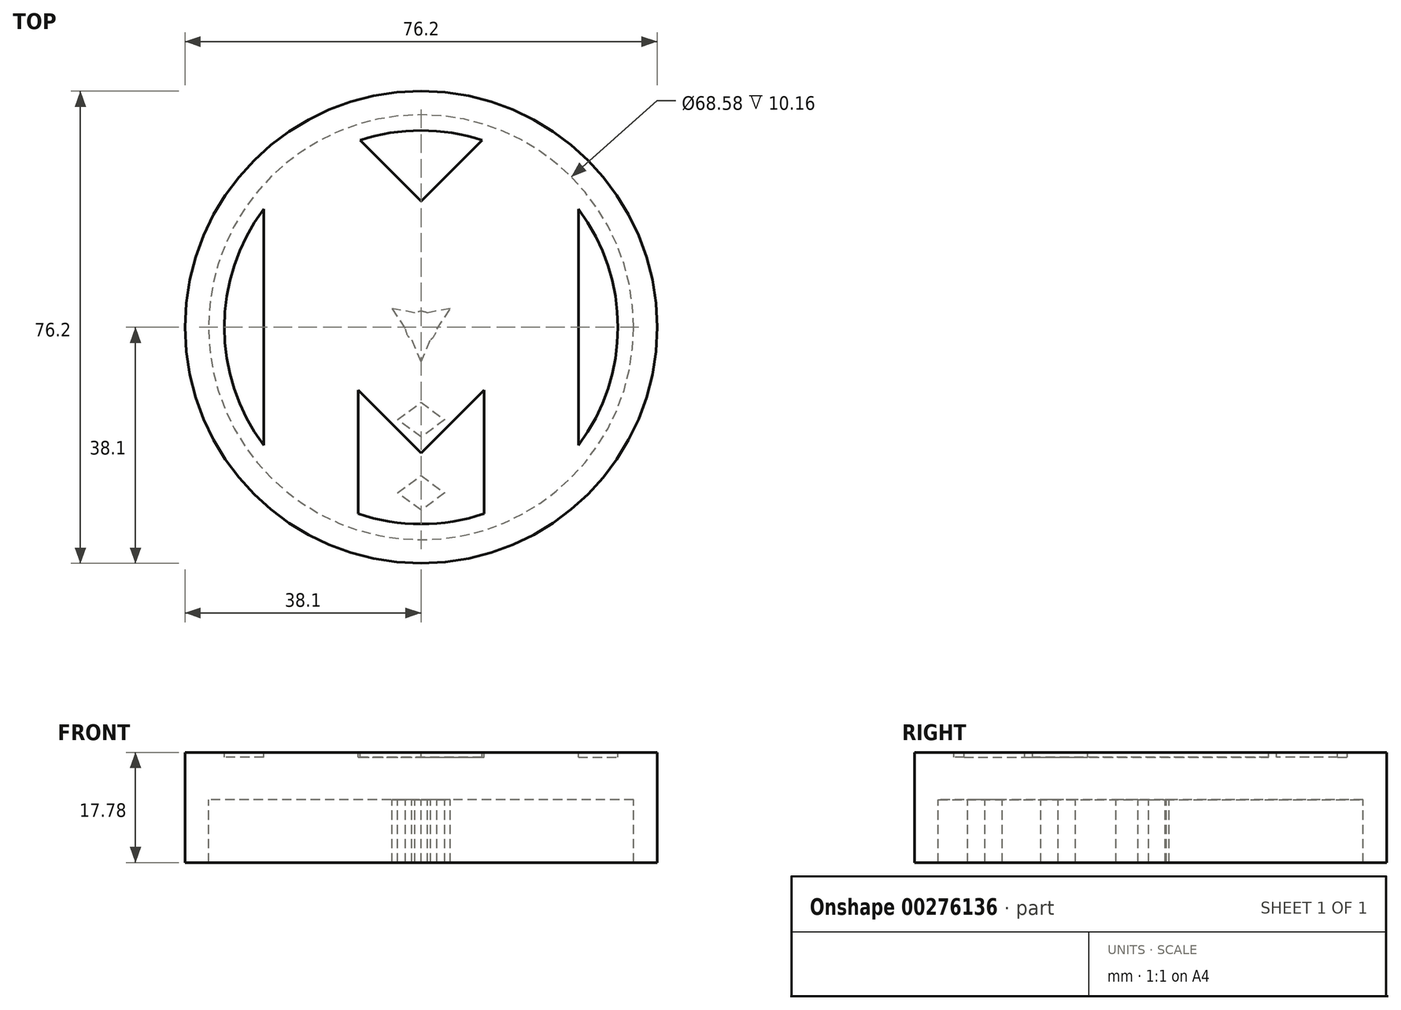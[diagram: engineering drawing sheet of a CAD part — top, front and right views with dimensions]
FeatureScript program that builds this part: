
annotation { "Feature Type Name" : "Feature", "Feature Type Description" : "" }
export const myFeature = defineFeature(function(context is Context, id is Id, definition is map)
    precondition{}
    {
        {
            var Q0;
            Q0=qCreatedBy(makeId("Top.planeOp"),FACE);
            var sketch = newSketch(context, id + "F0", { "sketchPlane" : qUnion([Q0])});
            skCircle(sketch, "E0", {"center": v(0, 0) * mm, "radius": 34.3 * mm});
            skCircle(sketch, "E1", {"center": v(0, 0) * mm, "radius": 38.1 * mm});
            skSolve(sketch);
        }
        {
            var Q0;
            Q0=makeQuery(id+"F0.imprint","IMPRINT",FACE,{"disambiguationData":[TD([[makeQuery(id+"F0.imprint","IMPRINT",EDGE,{"derivedFrom":sQuery(id+"F0.wireOp",EDGE,"E0")}),-1.0]])]});
            var Q1;
            Q1=makeQuery(id+"F0.imprint","IMPRINT",FACE,{"disambiguationData":[TD([[makeQuery(id+"F0.imprint","IMPRINT",EDGE,{"derivedFrom":sQuery(id+"F0.wireOp",EDGE,"E0")}),1.0]])]});
            extrude(context, id + "F1", {"entities" : qUnion([Q0, Q1]), "oppositeDirection" : true, "depth" : 7.62 * mm, "offsetDistance" : 25.4 * mm});
        }
        {
            var Q0;
            Q0=makeQuery(id+"F0.imprint","IMPRINT",FACE,{"disambiguationData":[TD([[makeQuery(id+"F0.imprint","IMPRINT",EDGE,{"derivedFrom":sQuery(id+"F0.wireOp",EDGE,"E0")}),-1.0]])]});
            extrude(context, id + "F2", {"entities" : qUnion([Q0]), "operationType" : NewBodyOperationType.ADD, "oppositeDirection" : true, "depth" : 17.78 * mm, "offsetDistance" : 25.4 * mm});
        }
        {
            var Q0;
            Q0=makeQuery(id+"F1.opExtrude","CAP_FACE",FACE,{"disambiguationData":[OSD([sQuery(id+"F0.wireOp",EDGE,"E1")])],"isStart":false});
            var sketch = newSketch(context, id + "F3", { "sketchPlane" : qUnion([Q0])});
            skArc(sketch, "E2", {"start": v(-1, -2.34) * mm, "mid": v(0, -2.54) * mm, "end": v(1, -2.34) * mm});
            skLineSegment(sketch, "E3", {"start": v(0, 5.59) * mm, "end": v(1.52, 2.03) * mm});
            skLineSegment(sketch, "E4", {"start": v(2.52, 0.3) * mm, "end": v(4.7, -3) * mm});
            skLineSegment(sketch, "E5", {"start": v(4.7, -3) * mm, "end": v(1, -2.34) * mm});
            skPoint(sketch, "E6", {"position": v(1.27, 2.8) * mm});
            skLineSegment(sketch, "E7", {"start": v(-4.7, -3) * mm, "end": v(-2.52, 0.3) * mm});
            skLineSegment(sketch, "E8.trimOffspring", {"start": v(-1.52, 2.03) * mm, "end": v(0, 5.59) * mm});
            skPoint(sketch, "E9.orphan", {"position": v(-2.54, 0) * mm});
            skLineSegment(sketch, "E10.trimOffspring", {"start": v(-1, -2.34) * mm, "end": v(-4.7, -3) * mm});
            skArc(sketch, "E11.trimOffspring", {"start": v(2.52, 0.3) * mm, "mid": v(2.2, 1.27) * mm, "end": v(1.52, 2.03) * mm});
            skPoint(sketch, "E12.orphan", {"position": v(1.27, 2.2) * mm});
            skPoint(sketch, "E13.orphan", {"position": v(2.54, 0) * mm});
            skArc(sketch, "E14.trimOffspring", {"start": v(-1.52, 2.03) * mm, "mid": v(-2.2, 1.27) * mm, "end": v(-2.52, 0.3) * mm});
            skLineSegment(sketch, "E15", {"start": v(0, 17.72) * mm, "end": v(-3.8, 14.92) * mm});
            skLineSegment(sketch, "E16", {"start": v(-3.8, 14.92) * mm, "end": v(0, 12.13) * mm});
            skLineSegment(sketch, "E17", {"start": v(0, 12.13) * mm, "end": v(3.8, 14.92) * mm});
            skLineSegment(sketch, "E18", {"start": v(3.8, 14.92) * mm, "end": v(0, 17.72) * mm});
            skLineSegment(sketch, "E19", {"start": v(0, 29.53) * mm, "end": v(-3.8, 26.73) * mm});
            skLineSegment(sketch, "E20", {"start": v(-3.8, 26.73) * mm, "end": v(0, 23.94) * mm});
            skLineSegment(sketch, "E21", {"start": v(0, 23.94) * mm, "end": v(3.8, 26.73) * mm});
            skLineSegment(sketch, "E22", {"start": v(3.8, 26.73) * mm, "end": v(0, 29.53) * mm});
            skSolve(sketch);
        }
        {
            var Q0;
            Q0=makeQuery(id+"F3.imprint","IMPRINT",FACE,{"disambiguationData":[TD([[makeQuery(id+"F3.imprint","IMPRINT",EDGE,{"derivedFrom":sQuery(id+"F3.wireOp",EDGE,"E2")}),1.0]])]});
            extrude(context, id + "F4", {"entities" : qUnion([Q0]), "operationType" : NewBodyOperationType.ADD, "depth" : 10.16 * mm, "offsetDistance" : 25.4 * mm});
        }
        {
            var Q0;
            Q0=makeQuery(id+"F3.imprint","IMPRINT",FACE,{"disambiguationData":[TD([[makeQuery(id+"F3.imprint","IMPRINT",EDGE,{"derivedFrom":sQuery(id+"F3.wireOp",EDGE,"E15")}),1.0]])]});
            extrude(context, id + "F5", {"entities" : qUnion([Q0]), "operationType" : NewBodyOperationType.ADD, "depth" : 10.16 * mm, "offsetDistance" : 25.4 * mm});
        }
        {
            var Q0;
            Q0=makeQuery(id+"F3.imprint","IMPRINT",FACE,{"disambiguationData":[TD([[makeQuery(id+"F3.imprint","IMPRINT",EDGE,{"derivedFrom":sQuery(id+"F3.wireOp",EDGE,"E19")}),1.0]])]});
            extrude(context, id + "F6", {"entities" : qUnion([Q0]), "operationType" : NewBodyOperationType.ADD, "depth" : 10.16 * mm, "offsetDistance" : 25.4 * mm});
        }
        {
            var Q0;
            Q0=makeQuery(id+"F1.opExtrude","CAP_FACE",FACE,{"disambiguationData":[OSD([sQuery(id+"F0.wireOp",EDGE,"E1")])],"isStart":true});
            var sketch = newSketch(context, id + "F7", { "sketchPlane" : qUnion([Q0])});
            skArc(sketch, "E23", {"start": v(-10.16, -30.08) * mm, "mid": v(0, -31.75) * mm, "end": v(10.16, -30.08) * mm});
            skLineSegment(sketch, "E24", {"start": v(-25.4, -19.05) * mm, "end": v(-25.4, 19.05) * mm});
            skLineSegment(sketch, "E25", {"start": v(25.4, 19.05) * mm, "end": v(25.4, -19.05) * mm});
            skLineSegment(sketch, "E26", {"start": v(-10.16, -30.08) * mm, "end": v(-10.16, -10.16) * mm});
            skLineSegment(sketch, "E27", {"start": v(-10.16, -10.16) * mm, "end": v(0, -20.32) * mm});
            skLineSegment(sketch, "E28", {"start": v(0, -20.32) * mm, "end": v(10.16, -10.16) * mm});
            skLineSegment(sketch, "E29", {"start": v(10.16, -10.16) * mm, "end": v(10.16, -30.08) * mm});
            skLineSegment(sketch, "E30", {"start": v(-9.86, 30.18) * mm, "end": v(0, 20.32) * mm});
            skLineSegment(sketch, "E31", {"start": v(0, 20.32) * mm, "end": v(9.86, 30.18) * mm});
            skArc(sketch, "E32.trimOffspring", {"start": v(-25.4, 19.05) * mm, "mid": v(-31.75, 0) * mm, "end": v(-25.4, -19.05) * mm});
            skArc(sketch, "E33.trimOffspring", {"start": v(9.86, 30.18) * mm, "mid": v(0, 31.75) * mm, "end": v(-9.86, 30.18) * mm});
            skArc(sketch, "E34.trimOffspring", {"start": v(25.4, -19.05) * mm, "mid": v(31.75, 0) * mm, "end": v(25.4, 19.05) * mm});
            skPoint(sketch, "E35.orphan", {"position": v(-10.16, 30.48) * mm});
            skPoint(sketch, "E36.orphan", {"position": v(10.16, 30.48) * mm});
            skSolve(sketch);
        }
        {
            var Q0;
            Q0 = qSketchRegion(id + "F7", true);
            extrude(context, id + "F8", {"entities" : qUnion([Q0]), "operationType" : NewBodyOperationType.REMOVE, "oppositeDirection" : true, "depth" : 0.76 * mm, "offsetDistance" : 25.4 * mm});
        }
    });
